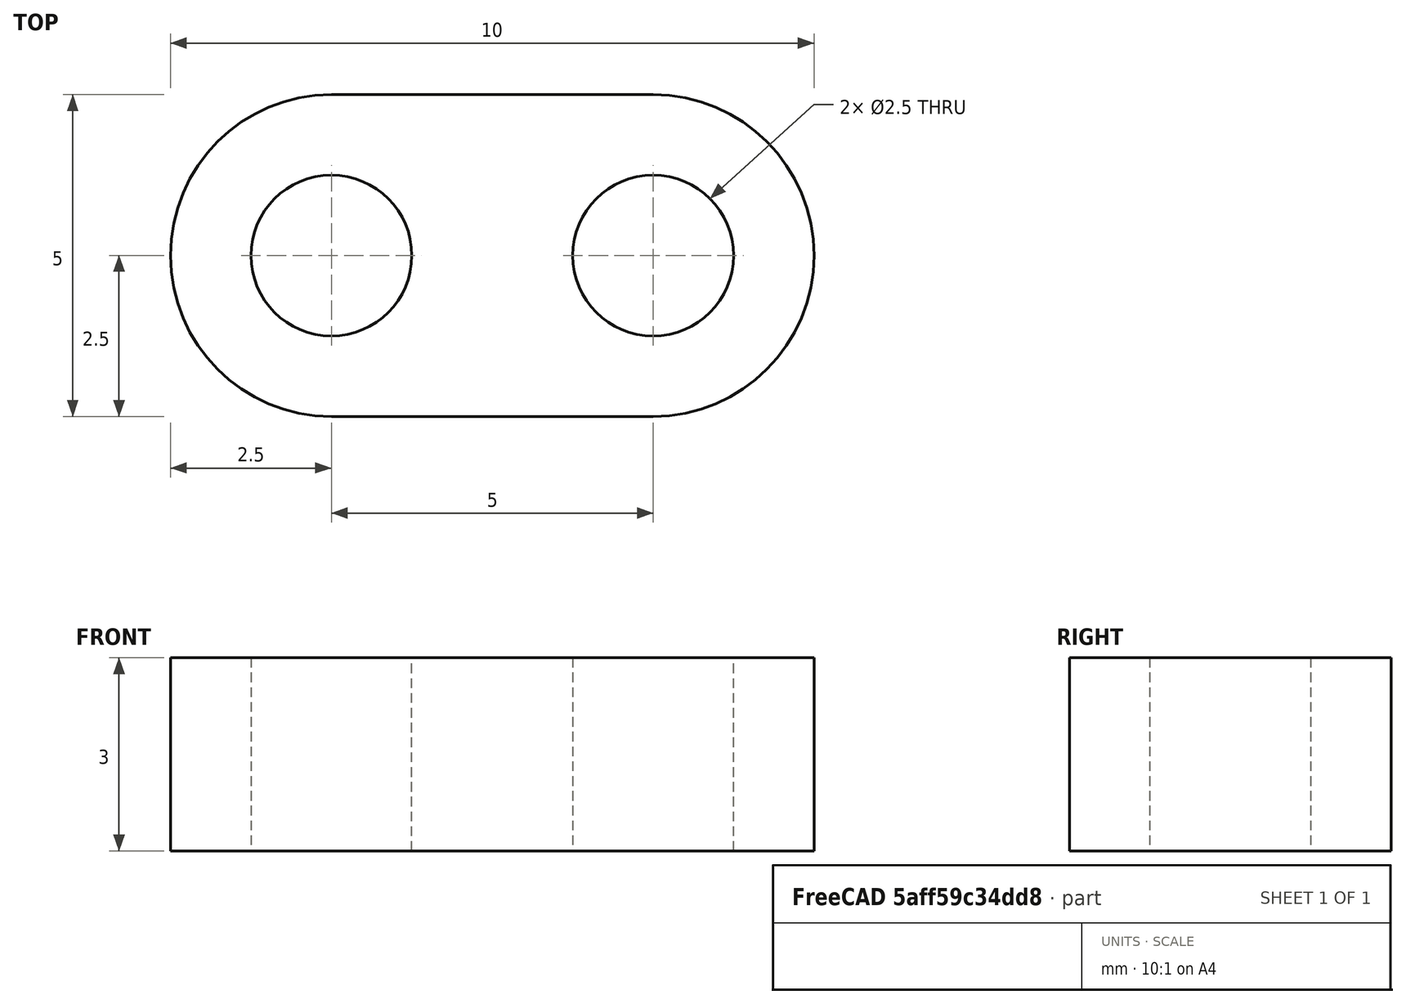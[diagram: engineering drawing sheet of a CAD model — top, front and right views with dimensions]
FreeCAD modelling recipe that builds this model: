
FCSTD DOCUMENT  (FreeCAD 0.19R)
Label: m2-universalboard-connector
License: All rights reserved
LicenseURL: http://en.wikipedia.org/wiki/All_rights_reserved
objects: Sketcher::SketchObject×1, PartDesign::Pad×1, PartDesign::Body×1
note: 4 computed .brp shape members not serialized (recipe doc carries the construction recipe); baked Part::Feature solids carry a one-line shape summary decoded from their .brp

FEATURE [Sketcher::SketchObject] Sketch
  FullyConstrained = true
  MapMode = 5
  Support = -> [XY_Plane]
  sketch-geometry (6):
    g0: ArcOfCircle CenterX=-2.5 CenterY=0 CenterZ=0 NormalX=0 NormalY=0 NormalZ=1 AngleXU=0 Radius=2.5 StartAngle=1.5708 EndAngle=4.71239
    g1: ArcOfCircle CenterX=2.5 CenterY=0 CenterZ=0 NormalX=0 NormalY=0 NormalZ=1 AngleXU=0 Radius=2.5 StartAngle=4.71239 EndAngle=7.85398
    g2: LineSegment StartX=-2.5 StartY=-2.5 StartZ=0 EndX=2.5 EndY=-2.5 EndZ=0
    g3: LineSegment StartX=-2.5 StartY=2.5 StartZ=0 EndX=2.5 EndY=2.5 EndZ=0
    g4: Circle CenterX=-2.5 CenterY=0 CenterZ=0 NormalX=0 NormalY=0 NormalZ=1 AngleXU=0 Radius=1.25
    g5: Circle CenterX=2.5 CenterY=0 CenterZ=0 NormalX=0 NormalY=0 NormalZ=1 AngleXU=0 Radius=1.25
  constraints (13):
    c: Tangent(g0,g3) = 1.5708
    c: Tangent(g0,g2) = -1.5708
    c: Tangent(g2,g1) = -1.5708
    c: Tangent(g3,g1) = 1.5708
    c: Horizontal(g2)
    c: Equal(g0,g1)
    c: Symmetric(g1,g0,g-1)
    c: Coincident(g4,g0)
    c: Coincident(g5,g1)
    c: Diameter(g5) = 2.5
    c: Diameter(g4) = 2.5
    c: Diameter(g1) = 5
    c: DistanceX(g0,g1) = 5
FEATURE [PartDesign::Pad] Pad
  Direction = (1,1,1)
  Length = 3
  Length2 = 100
  Profile = -> Sketch
  Type = 0
FEATURE [PartDesign::Body] Body
  Group = -> [Sketch,Pad]
  Origin = -> Origin
  Tip = -> Pad
